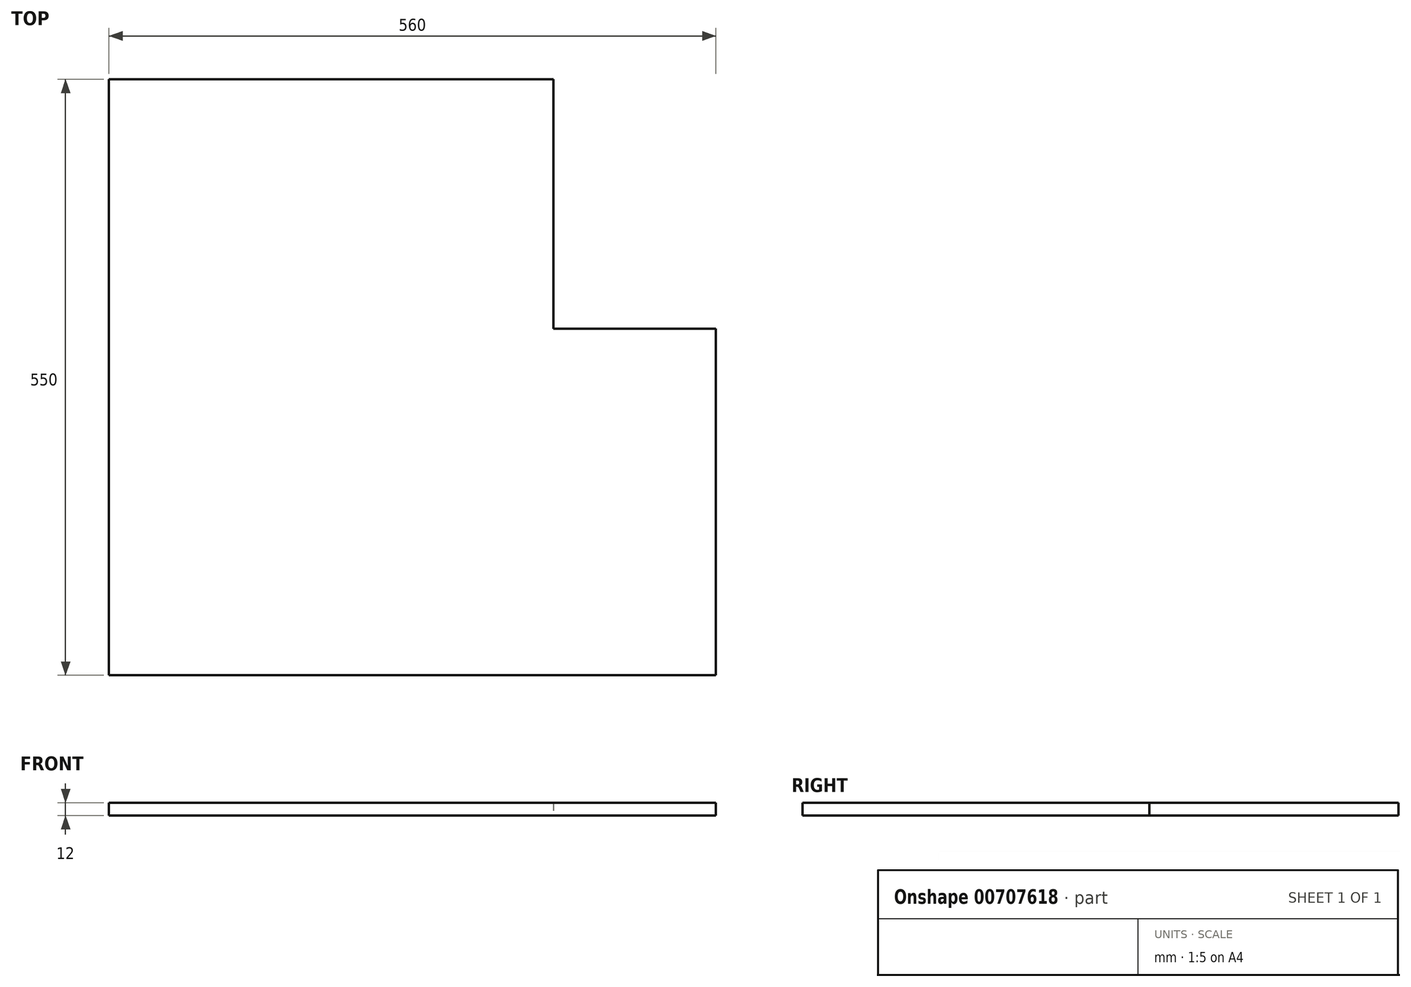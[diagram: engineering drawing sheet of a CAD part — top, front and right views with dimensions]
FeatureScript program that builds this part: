
annotation { "Feature Type Name" : "Feature", "Feature Type Description" : "" }
export const myFeature = defineFeature(function(context is Context, id is Id, definition is map)
    precondition{}
    {
        {
            var Q0;
            Q0=qCreatedBy(makeId("Top.planeOp"),FACE);
            var sketch = newSketch(context, id + "F0", { "sketchPlane" : qUnion([Q0])});
            skLineSegment(sketch, "E0.bottom", {"start": v(0, 550) * mm, "end": v(410, 550) * mm});
            skLineSegment(sketch, "E0.top", {"start": v(0, 0) * mm, "end": v(560, 0) * mm});
            skLineSegment(sketch, "E0.left", {"start": v(0, 550) * mm, "end": v(0, 0) * mm});
            skLineSegment(sketch, "E0.right", {"start": v(560, 320) * mm, "end": v(560, 0) * mm});
            skLineSegment(sketch, "E1", {"start": v(410, 550) * mm, "end": v(410, 320) * mm});
            skLineSegment(sketch, "E2", {"start": v(560, 320) * mm, "end": v(410, 320) * mm});
            skSolve(sketch);
        }
        {
            var Q0;
            Q0=makeQuery(id+"F0.imprint","IMPRINT",FACE,{"disambiguationData":[TD([[makeQuery(id+"F0.imprint","IMPRINT",EDGE,{"derivedFrom":sQuery(id+"F0.wireOp",EDGE,"E0.bottom")}),-1.0]])]});
            extrude(context, id + "F1", {"entities" : qUnion([Q0]), "depth" : 12 * mm, "offsetDistance" : 25.4 * mm});
        }
    });
